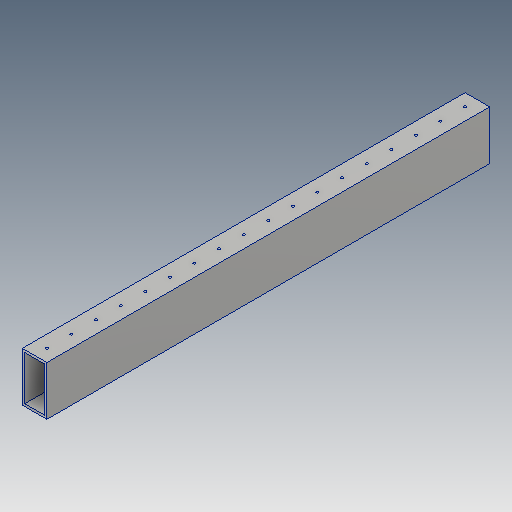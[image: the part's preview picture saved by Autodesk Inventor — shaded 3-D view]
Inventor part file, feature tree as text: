
AUTODESK INVENTOR PART (.ipt)
format: ipt  version: 2018 (Build 220112000, 112)  size: 137,728 bytes
history: native  units: in
note: dims shown in document units (in); Inventor stores cm internally (conversion verified against a paired STEP export)
features: sketch x2, extrude x1, shell x1, hole x1
ambient origin geometry x8: Origin, YZ Plane, XZ Plane, XY Plane, X Axis, Y Axis, Z Axis, Center Point
bodies: Solid1 (feature_tree)
feature tree (5):
  extrude  "Extrusion1"  Depth=2.0in
  shell  "Shell1"  Thickness=18.0in
  hole  "Hole1"  [1 undecoded]
  sketch  "Sketch1"  dims[d0=1.0in d1=2.0in d2=18.0in d3=0.0in]
  sketch  "Sketch2"  dims[d4=0.1in d5=0.5in d6=0.5in d7=12.2047in d9=1.0in d10=0.3937in d12=1.0in d14=0.1in d15=0.75in d16=0.375in d17=0.25in d18=0.5635in d19=2.0in d20=0.8108in]
note: 1 required parameter value undecoded (feature->parameter linkage not recoverable at this tier; creation-order binding heuristic only, values carry confidence <= 0.55)
